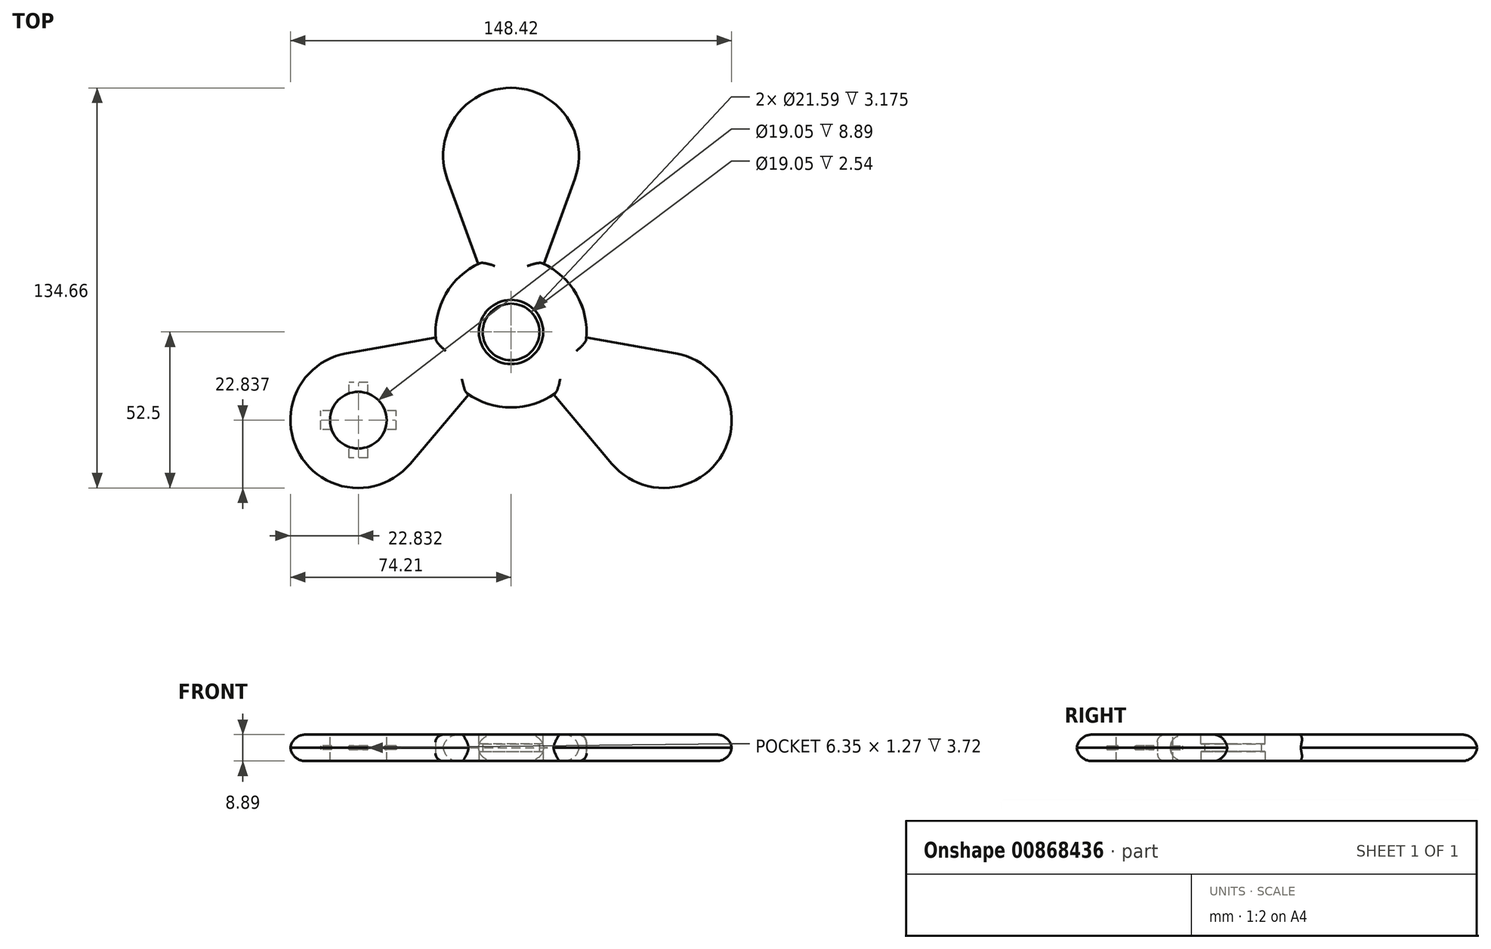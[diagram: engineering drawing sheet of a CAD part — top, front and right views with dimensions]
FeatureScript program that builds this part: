
annotation { "Feature Type Name" : "Feature", "Feature Type Description" : "" }
export const myFeature = defineFeature(function(context is Context, id is Id, definition is map)
    precondition{}
    {
        {
            var Q0;
            Q0=qCreatedBy(makeId("Top.planeOp"),FACE);
            var sketch = newSketch(context, id + "F0", { "sketchPlane" : qUnion([Q0])});
            skArc(sketch, "E0", {"start": v(-11.07, 22.86) * mm, "mid": v(-22, 12.7) * mm, "end": v(-25.33, -1.84) * mm});
            skLineSegment(sketch, "E1", {"start": v(0, 0) * mm, "end": v(0, 85.3) * mm, "construction": true});
            skLineSegment(sketch, "E2", {"start": v(0, 0) * mm, "end": v(73.9, -42.67) * mm, "construction": true});
            skLineSegment(sketch, "E3", {"start": v(0, 0) * mm, "end": v(-85.25, -49.22) * mm, "construction": true});
            skLineSegment(sketch, "E4", {"start": v(-11.07, 22.86) * mm, "end": v(-21.5, 51.5) * mm});
            skLineSegment(sketch, "E5", {"start": v(11.07, 22.86) * mm, "end": v(21.5, 51.5) * mm});
            skArc(sketch, "E6", {"start": v(21.5, 51.5) * mm, "mid": v(0, 82.2) * mm, "end": v(-21.5, 51.5) * mm});
            skArc(sketch, "E7.1.0", {"start": v(-55.35, -7.13) * mm, "mid": v(-71.19, -41.1) * mm, "end": v(-33.85, -44.37) * mm});
            skLineSegment(sketch, "E7.1.1", {"start": v(-25.33, -1.84) * mm, "end": v(-55.35, -7.13) * mm});
            skLineSegment(sketch, "E7.1.2", {"start": v(-14.26, -21.02) * mm, "end": v(-33.85, -44.37) * mm});
            skArc(sketch, "E7.2.0", {"start": v(33.85, -44.37) * mm, "mid": v(71.19, -41.1) * mm, "end": v(55.35, -7.13) * mm});
            skLineSegment(sketch, "E7.2.1", {"start": v(14.26, -21.02) * mm, "end": v(33.85, -44.37) * mm});
            skLineSegment(sketch, "E7.2.2", {"start": v(25.33, -1.84) * mm, "end": v(55.35, -7.13) * mm});
            skCircle(sketch, "E8", {"center": v(0, 0) * mm, "radius": 9.53 * mm});
            skArc(sketch, "E9.trimOffspring", {"start": v(25.33, -1.84) * mm, "mid": v(22, 12.7) * mm, "end": v(11.07, 22.86) * mm});
            skArc(sketch, "E10.trimOffspring", {"start": v(-14.26, -21.02) * mm, "mid": v(0, -25.4) * mm, "end": v(14.26, -21.02) * mm});
            skSolve(sketch);
        }
        {
            var Q0;
            Q0 = qSketchRegion(id + "F0", true);
            extrude(context, id + "F1", {"entities" : qUnion([Q0]), "depth" : 8.9 * mm, "offsetDistance" : 25.4 * mm});
        }
        {
            var Q0;
            Q0=makeQuery(id+"F1.opExtrude","CAP_EDGE",EDGE,{"disambiguationData":[OSD([sQuery(id+"F0.wireOp",EDGE,"E7.1.0")])],"isStart":false});
            var Q1;
            Q1=makeQuery(id+"F1.opExtrude","CAP_EDGE",EDGE,{"disambiguationData":[OSD([sQuery(id+"F0.wireOp",EDGE,"E7.1.0")])],"isStart":true});
            var Q2;
            Q2=makeQuery(id+"F1.opExtrude","CAP_EDGE",EDGE,{"disambiguationData":[OSD([sQuery(id+"F0.wireOp",EDGE,"E6")])],"isStart":false});
            var Q3;
            Q3=makeQuery(id+"F1.opExtrude","CAP_EDGE",EDGE,{"disambiguationData":[OSD([sQuery(id+"F0.wireOp",EDGE,"E6")])],"isStart":true});
            var Q4;
            Q4=makeQuery(id+"F1.opExtrude","CAP_EDGE",EDGE,{"disambiguationData":[OSD([sQuery(id+"F0.wireOp",EDGE,"E7.2.0")])],"isStart":false});
            var Q5;
            Q5=makeQuery(id+"F1.opExtrude","CAP_EDGE",EDGE,{"disambiguationData":[OSD([sQuery(id+"F0.wireOp",EDGE,"E7.2.0")])],"isStart":true});
            fillet(context, id + "F2", {"entities" : qUnion([Q0, Q1, Q2, Q3, Q4, Q5]), "radius" : 5.08 * mm, "tangentPropagation" : true, "allowEdgeOverflow" : false});
        }
        {
            var Q0;
            Q0=makeQuery(id+"F1.opExtrude","CAP_EDGE",EDGE,{"disambiguationData":[OSD([sQuery(id+"F0.wireOp",EDGE,"E9.trimOffspring")])],"isStart":false});
            var Q1;
            Q1=makeQuery(id+"F1.opExtrude","CAP_EDGE",EDGE,{"disambiguationData":[OSD([sQuery(id+"F0.wireOp",EDGE,"E9.trimOffspring")])],"isStart":true});
            var Q2;
            Q2=makeQuery(id+"F1.opExtrude","CAP_EDGE",EDGE,{"disambiguationData":[OSD([sQuery(id+"F0.wireOp",EDGE,"E0")])],"isStart":true});
            var Q3;
            Q3=makeQuery(id+"F1.opExtrude","CAP_EDGE",EDGE,{"disambiguationData":[OSD([sQuery(id+"F0.wireOp",EDGE,"E10.trimOffspring")])],"isStart":true});
            var Q4;
            Q4=makeQuery(id+"F1.opExtrude","CAP_EDGE",EDGE,{"disambiguationData":[OSD([sQuery(id+"F0.wireOp",EDGE,"E10.trimOffspring")])],"isStart":false});
            var Q5;
            Q5=makeQuery(id+"F1.opExtrude","CAP_EDGE",EDGE,{"disambiguationData":[OSD([sQuery(id+"F0.wireOp",EDGE,"E0")])],"isStart":false});
            fillet(context, id + "F3", {"entities" : qUnion([Q0, Q1, Q2, Q3, Q4, Q5]), "radius" : 2.54 * mm, "tangentPropagation" : true, "allowEdgeOverflow" : false});
        }
        {
            var Q0;
            Q0=makeQuery(id+"F1.opExtrude","CAP_FACE",FACE,{"disambiguationData":[OSD([sQuery(id+"F0.wireOp",EDGE,"E0"),sQuery(id+"F0.wireOp",EDGE,"E4"),sQuery(id+"F0.wireOp",EDGE,"E5"),sQuery(id+"F0.wireOp",EDGE,"E6"),sQuery(id+"F0.wireOp",EDGE,"E7.1.0"),sQuery(id+"F0.wireOp",EDGE,"E7.1.1"),sQuery(id+"F0.wireOp",EDGE,"E7.1.2"),sQuery(id+"F0.wireOp",EDGE,"E7.2.0"),sQuery(id+"F0.wireOp",EDGE,"E7.2.1"),sQuery(id+"F0.wireOp",EDGE,"E7.2.2"),sQuery(id+"F0.wireOp",EDGE,"E8"),sQuery(id+"F0.wireOp",EDGE,"E9.trimOffspring"),sQuery(id+"F0.wireOp",EDGE,"E10.trimOffspring")])],"isStart":false});
            var sketch = newSketch(context, id + "F4", { "sketchPlane" : qUnion([Q0])});
            skCircle(sketch, "E11", {"center": v(0, 0) * mm, "radius": 10.8 * mm});
            skSolve(sketch);
        }
        {
            var Q0;
            Q0 = qSketchRegion(id + "F4", true);
            extrude(context, id + "F5", {"entities" : qUnion([Q0]), "operationType" : NewBodyOperationType.REMOVE, "oppositeDirection" : true, "depth" : 3.17 * mm, "offsetDistance" : 25.4 * mm});
        }
        {
            var Q0;
            Q0=makeQuery(id+"F1.opExtrude","CAP_FACE",FACE,{"disambiguationData":[OSD([sQuery(id+"F0.wireOp",EDGE,"E0"),sQuery(id+"F0.wireOp",EDGE,"E4"),sQuery(id+"F0.wireOp",EDGE,"E5"),sQuery(id+"F0.wireOp",EDGE,"E6"),sQuery(id+"F0.wireOp",EDGE,"E7.1.0"),sQuery(id+"F0.wireOp",EDGE,"E7.1.1"),sQuery(id+"F0.wireOp",EDGE,"E7.1.2"),sQuery(id+"F0.wireOp",EDGE,"E7.2.0"),sQuery(id+"F0.wireOp",EDGE,"E7.2.1"),sQuery(id+"F0.wireOp",EDGE,"E7.2.2"),sQuery(id+"F0.wireOp",EDGE,"E8"),sQuery(id+"F0.wireOp",EDGE,"E9.trimOffspring"),sQuery(id+"F0.wireOp",EDGE,"E10.trimOffspring")])],"isStart":true});
            var sketch = newSketch(context, id + "F6", { "sketchPlane" : qUnion([Q0])});
            skCircle(sketch, "E12", {"center": v(0, 0) * mm, "radius": 10.8 * mm});
            skSolve(sketch);
        }
        {
            var Q0;
            Q0 = qSketchRegion(id + "F6", true);
            extrude(context, id + "F7", {"entities" : qUnion([Q0]), "operationType" : NewBodyOperationType.REMOVE, "oppositeDirection" : true, "depth" : 3.17 * mm, "offsetDistance" : 25.4 * mm});
        }
        {
            var Q0;
            Q0=makeQuery(id+"F1.opExtrude","CAP_FACE",FACE,{"disambiguationData":[OSD([sQuery(id+"F0.wireOp",EDGE,"E0"),sQuery(id+"F0.wireOp",EDGE,"E4"),sQuery(id+"F0.wireOp",EDGE,"E5"),sQuery(id+"F0.wireOp",EDGE,"E6"),sQuery(id+"F0.wireOp",EDGE,"E7.1.0"),sQuery(id+"F0.wireOp",EDGE,"E7.1.1"),sQuery(id+"F0.wireOp",EDGE,"E7.1.2"),sQuery(id+"F0.wireOp",EDGE,"E7.2.0"),sQuery(id+"F0.wireOp",EDGE,"E7.2.1"),sQuery(id+"F0.wireOp",EDGE,"E7.2.2"),sQuery(id+"F0.wireOp",EDGE,"E8"),sQuery(id+"F0.wireOp",EDGE,"E9.trimOffspring"),sQuery(id+"F0.wireOp",EDGE,"E10.trimOffspring")])],"isStart":false});
            var sketch = newSketch(context, id + "F8", { "sketchPlane" : qUnion([Q0])});
            skCircle(sketch, "E13", {"center": v(-51.38, -29.66) * mm, "radius": 9.53 * mm});
            skSolve(sketch);
        }
        {
            var Q0;
            Q0 = qSketchRegion(id + "F8", true);
            extrude(context, id + "F9", {"entities" : qUnion([Q0]), "operationType" : NewBodyOperationType.REMOVE, "endBound" : BoundingType.THROUGH_ALL, "oppositeDirection" : true, "depth" : 25.4 * mm, "offsetDistance" : 25.4 * mm});
        }
        {
            var Q0;
            Q0=makeQuery(id+"F1.opExtrude","CAP_FACE",FACE,{"disambiguationData":[OSD([sQuery(id+"F0.wireOp",EDGE,"E0"),sQuery(id+"F0.wireOp",EDGE,"E4"),sQuery(id+"F0.wireOp",EDGE,"E5"),sQuery(id+"F0.wireOp",EDGE,"E6"),sQuery(id+"F0.wireOp",EDGE,"E7.1.0"),sQuery(id+"F0.wireOp",EDGE,"E7.1.1"),sQuery(id+"F0.wireOp",EDGE,"E7.1.2"),sQuery(id+"F0.wireOp",EDGE,"E7.2.0"),sQuery(id+"F0.wireOp",EDGE,"E7.2.1"),sQuery(id+"F0.wireOp",EDGE,"E7.2.2"),sQuery(id+"F0.wireOp",EDGE,"E8"),sQuery(id+"F0.wireOp",EDGE,"E9.trimOffspring"),sQuery(id+"F0.wireOp",EDGE,"E10.trimOffspring")])],"isStart":true});
            cPlane(context, id + "F10", {"entities" : qUnion([Q0]), "cplaneType" : CPlaneType.OFFSET, "offset" : 4.44 * mm, "oppositeDirection" : true, "width" : 152.4 * mm, "height" : 152.4 * mm});
        }
        {
            var Q0;
            Q0=qCreatedBy(id+"F10.planeOp",FACE);
            var sketch = newSketch(context, id + "F11", { "sketchPlane" : qUnion([Q0])});
            skLineSegment(sketch, "E14", {"start": v(-41.85, 29.66) * mm, "end": v(-60.9, 29.66) * mm, "construction": true});
            skLineSegment(sketch, "E15", {"start": v(-51.38, 39.19) * mm, "end": v(-51.38, 20.14) * mm, "construction": true});
            skLineSegment(sketch, "E16.bottom", {"start": v(-38.68, 32.84) * mm, "end": v(-48.2, 32.84) * mm});
            skLineSegment(sketch, "E16.top", {"start": v(-38.68, 26.49) * mm, "end": v(-48.2, 26.49) * mm});
            skLineSegment(sketch, "E16.left", {"start": v(-38.68, 32.84) * mm, "end": v(-38.68, 26.49) * mm});
            skLineSegment(sketch, "E16.right", {"start": v(-64.08, 32.84) * mm, "end": v(-64.08, 26.49) * mm});
            skLineSegment(sketch, "E17.bottom", {"start": v(-48.2, 42.36) * mm, "end": v(-54.55, 42.36) * mm});
            skLineSegment(sketch, "E17.top", {"start": v(-48.2, 16.96) * mm, "end": v(-54.55, 16.96) * mm});
            skLineSegment(sketch, "E17.left", {"start": v(-48.2, 42.36) * mm, "end": v(-48.2, 32.84) * mm});
            skLineSegment(sketch, "E17.right", {"start": v(-54.55, 42.36) * mm, "end": v(-54.55, 32.84) * mm});
            skLineSegment(sketch, "E18.trimOffspring", {"start": v(-48.2, 26.49) * mm, "end": v(-48.2, 16.96) * mm});
            skLineSegment(sketch, "E19.trimOffspring", {"start": v(-54.55, 32.84) * mm, "end": v(-64.08, 32.84) * mm});
            skLineSegment(sketch, "E20.trimOffspring", {"start": v(-54.55, 26.49) * mm, "end": v(-54.55, 16.96) * mm});
            skLineSegment(sketch, "E21.trimOffspring", {"start": v(-54.55, 26.49) * mm, "end": v(-64.08, 26.49) * mm});
            skSolve(sketch);
        }
        {
            var Q0;
            Q0 = qSketchRegion(id + "F11", true);
            extrude(context, id + "F12", {"entities" : qUnion([Q0]), "operationType" : NewBodyOperationType.REMOVE, "endBound" : BoundingType.SYMMETRIC, "oppositeDirection" : true, "depth" : 1.27 * mm, "offsetDistance" : 25.4 * mm});
        }
    });
